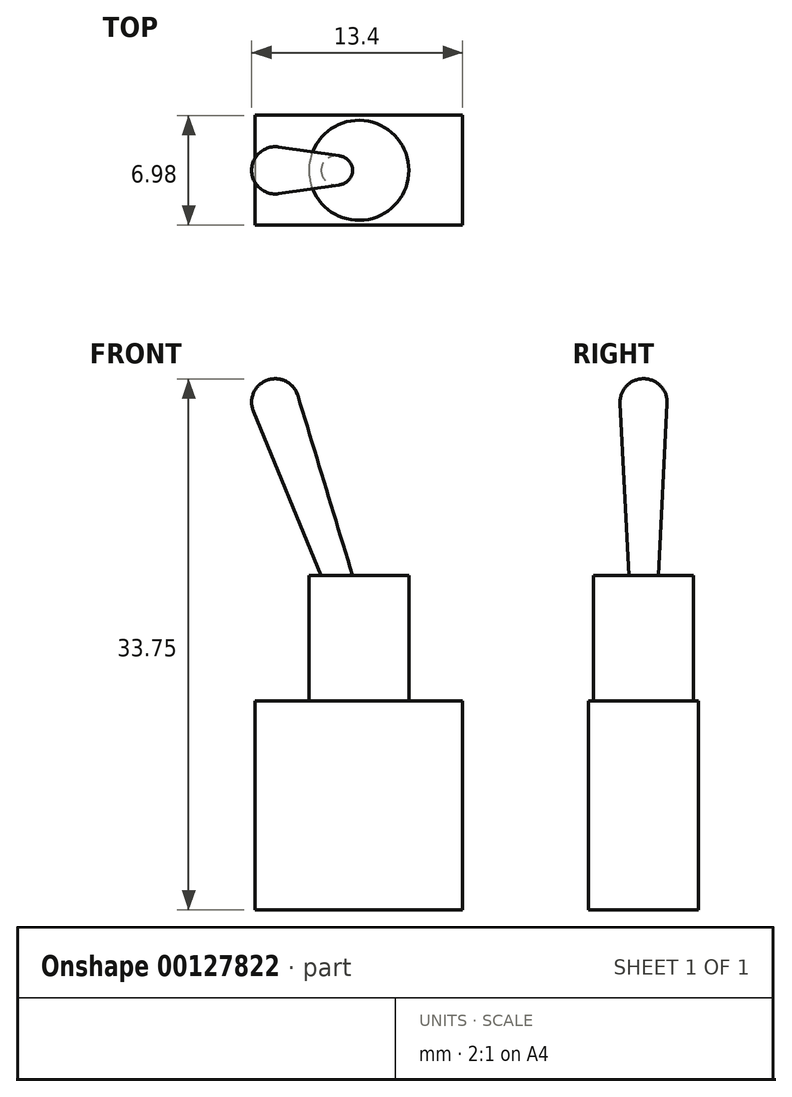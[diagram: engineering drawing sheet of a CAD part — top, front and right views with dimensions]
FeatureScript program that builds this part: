
annotation { "Feature Type Name" : "Feature", "Feature Type Description" : "" }
export const myFeature = defineFeature(function(context is Context, id is Id, definition is map)
    precondition{}
    {
        {
            var Q0;
            Q0=qCreatedBy(makeId("Top.planeOp"),FACE);
            var sketch = newSketch(context, id + "F0", { "sketchPlane" : qUnion([Q0])});
            skLineSegment(sketch, "E0.bottom", {"start": v(6.6, 3.5) * mm, "end": v(-6.6, 3.5) * mm});
            skLineSegment(sketch, "E0.top", {"start": v(6.6, -3.5) * mm, "end": v(-6.6, -3.5) * mm});
            skLineSegment(sketch, "E0.left", {"start": v(6.6, 3.5) * mm, "end": v(6.6, -3.5) * mm});
            skLineSegment(sketch, "E0.right", {"start": v(-6.6, 3.5) * mm, "end": v(-6.6, -3.5) * mm});
            skPoint(sketch, "E0.middle", {"position": v(0, 0) * mm});
            skSolve(sketch);
        }
        {
            var Q0;
            Q0=makeQuery(id+"F0.imprint","IMPRINT",FACE,{"disambiguationData":[TD([[makeQuery(id+"F0.imprint","IMPRINT",EDGE,{"derivedFrom":sQuery(id+"F0.wireOp",EDGE,"E0.bottom")}),1.0]])]});
            extrude(context, id + "F1", {"entities" : qUnion([Q0]), "depth" : 13.28 * mm});
        }
        {
            var Q0;
            Q0=makeQuery(id+"F1.opExtrude","CAP_FACE",FACE,{"disambiguationData":[OSD([sQuery(id+"F0.wireOp",EDGE,"E0.bottom"),sQuery(id+"F0.wireOp",EDGE,"E0.top"),sQuery(id+"F0.wireOp",EDGE,"E0.left"),sQuery(id+"F0.wireOp",EDGE,"E0.right")])],"isStart":false});
            var sketch = newSketch(context, id + "F2", { "sketchPlane" : qUnion([Q0])});
            skCircle(sketch, "E1", {"center": v(0, 0) * mm, "radius": 3.17 * mm});
            skSolve(sketch);
        }
        {
            var Q0;
            Q0=makeQuery(id+"F2.imprint","IMPRINT",FACE,{"disambiguationData":[TD([[makeQuery(id+"F2.imprint","IMPRINT",EDGE,{"derivedFrom":sQuery(id+"F2.wireOp",EDGE,"E1")}),1.0]])]});
            extrude(context, id + "F3", {"entities" : qUnion([Q0]), "operationType" : NewBodyOperationType.ADD, "depth" : 7.98 * mm});
        }
        {
            var Q0;
            Q0=makeQuery(id+"F1.opExtrude","SWEPT_FACE",FACE,{"disambiguationData":[OSD([sQuery(id+"F0.wireOp",EDGE,"E0.top")])]});
            cPlane(context, id + "F4", {"entities" : qUnion([Q0]), "cplaneType" : CPlaneType.OFFSET, "offset" : 3.5 * mm, "oppositeDirection" : true, "width" : 152.4 * mm, "height" : 152.4 * mm});
        }
        {
            var Q0;
            Q0=qCreatedBy(id+"F4.planeOp",FACE);
            var sketch = newSketch(context, id + "F5", { "sketchPlane" : qUnion([Q0])});
            skLineSegment(sketch, "E2.0", {"start": v(-1.39, 21.26) * mm, "end": v(-0.4, 21.26) * mm});
            skLineSegment(sketch, "E3", {"start": v(-0.4, 21.26) * mm, "end": v(-3.88, 32.7) * mm});
            skArc(sketch, "E4", {"start": v(-3.88, 32.7) * mm, "mid": v(-4.64, 33.6) * mm, "end": v(-5.82, 33.67) * mm});
            skLineSegment(sketch, "E5", {"start": v(-5.82, 33.67) * mm, "end": v(-1.39, 21.26) * mm});
            skSolve(sketch);
        }
        {
            var Q0;
            Q0=makeQuery(id+"F5.imprint","IMPRINT",FACE,{"disambiguationData":[TD([[makeQuery(id+"F5.imprint","IMPRINT",EDGE,{"derivedFrom":sQuery(id+"F5.wireOp",EDGE,"E2.0")}),1.0]])]});
            var Q1;
            Q1=sQuery(id+"F5.wireOp",EDGE,"E5");
            revolve(context, id + "F6", {"operationType" : NewBodyOperationType.ADD, "entities" : qUnion([Q0]), "axis" : qUnion([Q1]), "revolveType" : RevolveType.FULL});
        }
    });
